# Revit family: Verbundanker V, VA
name_source: partatom
category: HLS-Bauteile
revit_build: Autodesk Revit 2017 (Build: 20190507_1515(x64)
units: mm (PartAtom-declared; Revit-internal decimal feet)

## family parameters
Basisbauteil = Fläche
Beim Laden mit Abzugskörper schneiden = Nein
Bemaßung runder Anschluss = Durchmesser verwenden
Gemeinsam genutzt = Ja
Raumberechnungspunkt = Nein
Teiletyp = Normal

## types (3) — shared parameters
Fabrikat = MKT
Firma = MEFA Befestigungs- und Montagesysteme GmbH
L2 = 15 mm  [stored 0.0492126 ft]
Material = Edelstahl
Mengeneinheit = St
Vorgabe-Ansicht = 1219 mm
vpe = 10 St
zero-valued in all types: Länge Dübel

## per-type parameters (varying)
| type | Artikelnummer | Bohrerdurchmesser | Bohrlochtiefe | D | EAN | Gewicht | Gewicht pro Bauteil | Gewinde | Kurztext1 | Kurztext2 | L | L1 | Länge | Mutter | Unterlegscheibe | Verankerungstiefe |
| Gewindestange V-A  8- 20/110, VA4 | 222821101501 | 10 mm | 80 mm | 7 mm  [stored 0.0229659 ft] | 4043315019431 | 0.04 kg | 0.04 kg | M8 | Ankerstange V A M8 V4A | Länge 110 mm | 110 mm  [stored 0.360892 ft] | 95 mm | 110 mm  [stored 0.360892 ft] | Sechskantmutter : Sechskantmutter M8 | Unterlegscheibe : Unterlegscheibe 8.4x16x1.6 | 80 mm |
| Gewindestange V-A 10- 30/130, VA4 | 222821203501 | 12 mm | 90 mm | 8 mm  [stored 0.0262467 ft] | 4043315019882 | 0.08 kg | 0.08 kg | M10 | Ankerstange V A M10 V4A | Länge 130 mm | 130 mm  [stored 0.426509 ft] | 115 mm  [stored 0.377297 ft] | 130 mm  [stored 0.426509 ft] | Sechskantmutter : Sechskantmutter M10 | Unterlegscheibe : Unterlegscheibe 10.5x20x2 | 90 mm |
| Gewindestange V-A 12- 35/160, VA4 | 222821306501 | 14 mm | 110 mm | 10 mm  [stored 0.0328084 ft] | 4043315020659 | 0.14 kg | 0.14 kg | M12 | Ankerstange V A M12 V4A | Länge 160 mm | 160 mm  [stored 0.524934 ft] | 145 mm  [stored 0.475722 ft] | 160 mm  [stored 0.524934 ft] | Sechskantmutter : Sechskantmutter M12 | Unterlegscheibe : Unterlegscheibe 13x24x2.5 | 110 mm |

note: [stored X ft] marks values corroborated as IEEE doubles in the binary element streams (Revit-internal decimal feet)

## geometry (parser evidence)
native form markers: Sweep x3
no freeform markers — native parametric forms only
